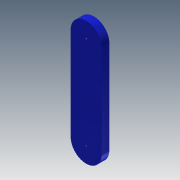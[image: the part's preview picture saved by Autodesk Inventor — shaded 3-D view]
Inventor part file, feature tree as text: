
AUTODESK INVENTOR PART (.ipt)
format: ipt  version: 2013 (Build 170138000, 138)  size: 101,376 bytes
history: native  units: mm
features: sketch x7, extrude x3
ambient origin geometry x8: Origin, YZ Plane, XZ Plane, XY Plane, X Axis, Y Axis, Z Axis, Center Point
bodies: Solid1 (feature_tree)
feature tree (10):
  extrude  "Extrusion1"  Depth=18.0mm
  extrude  "Extrusion2"  Depth=1.5mm TaperAngle=0.0deg
  sketch  "Sketch3"  dims[d5=3.0mm d6=3.0mm]
  sketch  "Sketch4"  dims[d7=2.0mm d8=0.0mm]
  sketch  "Sketch5"  dims[d13=0.2mm]
  sketch  "Sketch6"  dims[d14=0.2mm]
  extrude  "Extrusion3"  Depth=3.0mm
  sketch  "Sketch1"  dims[d0=6.0mm d1=18.0mm]
  sketch  "Sketch2"  dims[d2=6.0mm d3=1.5mm d4=0.0mm]
  sketch  "Sketch7"  dims[d15=1.5mm d16=0.0mm]
